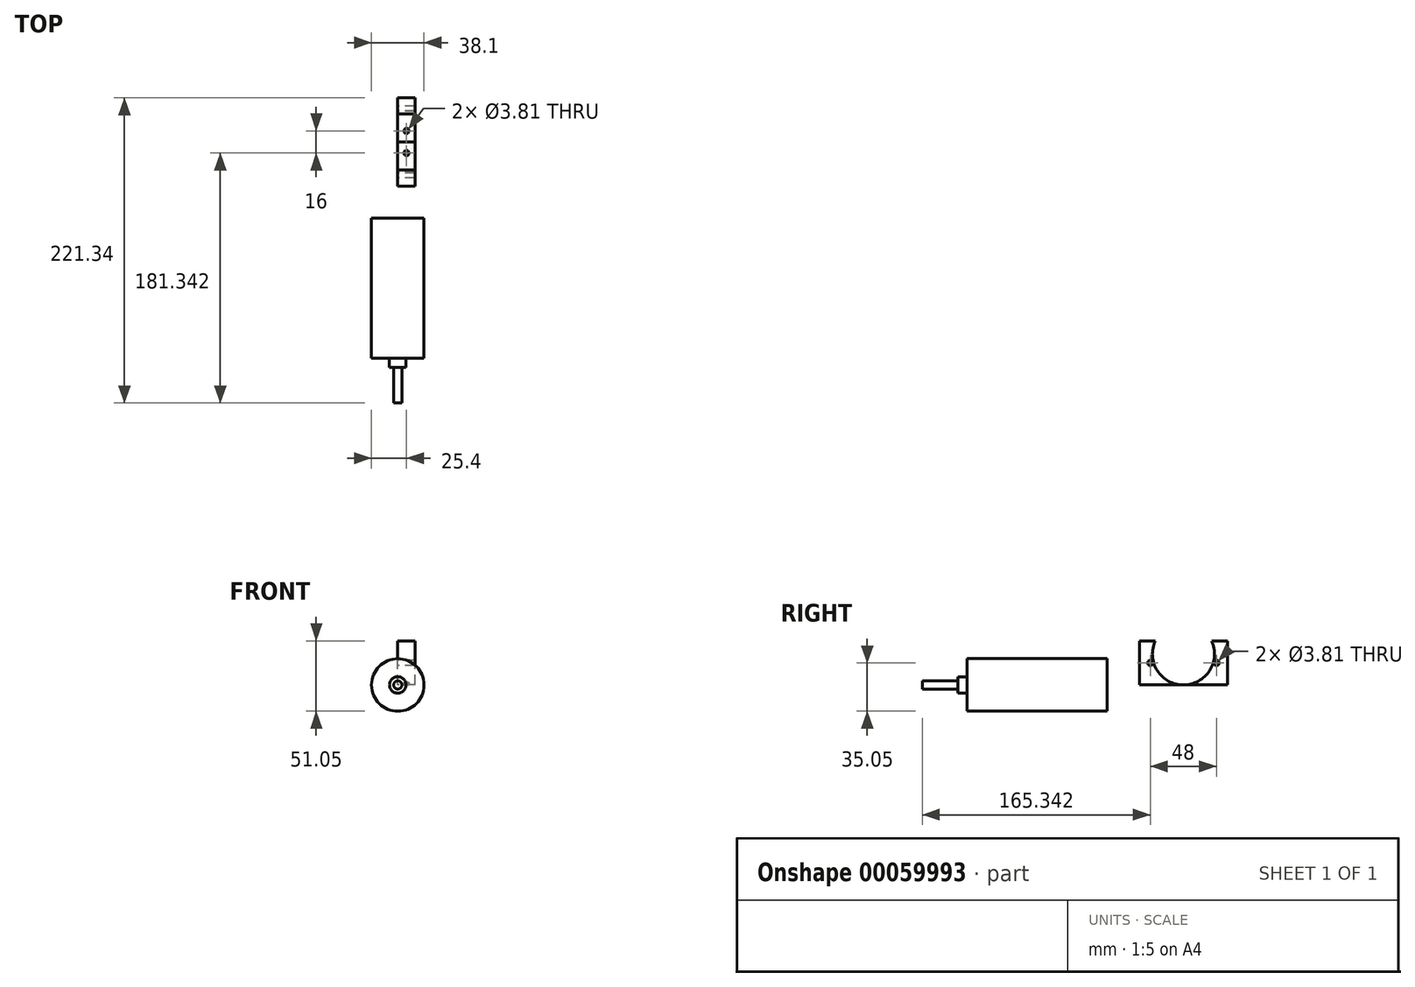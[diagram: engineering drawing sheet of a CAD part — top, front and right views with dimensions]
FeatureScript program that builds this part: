
annotation { "Feature Type Name" : "Feature", "Feature Type Description" : "" }
export const myFeature = defineFeature(function(context is Context, id is Id, definition is map)
    precondition{}
    {
        {
            var Q0;
            Q0=qCreatedBy(makeId("Front.planeOp"),FACE);
            var sketch = newSketch(context, id + "F0", { "sketchPlane" : qUnion([Q0])});
            skCircle(sketch, "E0", {"center": v(0, 0) * mm, "radius": 19.05 * mm});
            skSolve(sketch);
        }
        {
            var Q0;
            Q0=makeQuery(id+"F0.imprint","IMPRINT",FACE,{"disambiguationData":[TD([[makeQuery(id+"F0.imprint","IMPRINT",EDGE,{"derivedFrom":sQuery(id+"F0.wireOp",EDGE,"E0")}),1.0]])]});
            extrude(context, id + "F1", {"entities" : qUnion([Q0]), "depth" : 101.6 * mm});
        }
        {
            var Q0;
            Q0=makeQuery(id+"F1.opExtrude","CAP_FACE",FACE,{"disambiguationData":[OSD([sQuery(id+"F0.wireOp",EDGE,"E0")])],"isStart":false});
            var sketch = newSketch(context, id + "F2", { "sketchPlane" : qUnion([Q0])});
            skCircle(sketch, "E1", {"center": v(0, 0) * mm, "radius": 6 * mm});
            skSolve(sketch);
        }
        {
            var Q0;
            Q0=makeQuery(id+"F2.imprint","IMPRINT",FACE,{"disambiguationData":[TD([[makeQuery(id+"F2.imprint","IMPRINT",EDGE,{"derivedFrom":sQuery(id+"F2.wireOp",EDGE,"E1")}),1.0]])]});
            extrude(context, id + "F3", {"entities" : qUnion([Q0]), "operationType" : NewBodyOperationType.ADD, "depth" : 6.7 * mm});
        }
        {
            var Q0;
            Q0=makeQuery(id+"F3.opExtrude","CAP_FACE",FACE,{"disambiguationData":[OSD([sQuery(id+"F2.wireOp",EDGE,"E1")])],"isStart":false});
            var sketch = newSketch(context, id + "F4", { "sketchPlane" : qUnion([Q0])});
            skCircle(sketch, "E2", {"center": v(0, 0) * mm, "radius": 3 * mm});
            skSolve(sketch);
        }
        {
            var Q0;
            Q0=qSketchRegion(id+"F4",true);
            extrude(context, id + "F5", {"entities" : qUnion([Q0]), "operationType" : NewBodyOperationType.ADD, "depth" : 25.8 * mm});
        }
        {
            var Q0;
            Q0=qCreatedBy(makeId("Right.planeOp"),FACE);
            var sketch = newSketch(context, id + "F6", { "sketchPlane" : qUnion([Q0])});
            skLineSegment(sketch, "E3.bottom", {"start": v(23.24, 0) * mm, "end": v(87.24, 0) * mm});
            skLineSegment(sketch, "E3.top", {"start": v(23.24, 32) * mm, "end": v(87.24, 32) * mm});
            skLineSegment(sketch, "E3.left", {"start": v(23.24, 0) * mm, "end": v(23.24, 32) * mm});
            skLineSegment(sketch, "E3.right", {"start": v(87.24, 0) * mm, "end": v(87.24, 32) * mm});
            skCircle(sketch, "E4", {"center": v(55.24, 22.5) * mm, "radius": 18.5 * mm});
            skPoint(sketch, "E4.centerSnap0", {"position": v(55.24, 32) * mm});
            skCircle(sketch, "E5", {"center": v(55.24, 22.5) * mm, "radius": 22.5 * mm});
            skCircle(sketch, "E6", {"center": v(31.24, 16) * mm, "radius": 1.9 * mm});
            skPoint(sketch, "E6.centerSnap0", {"position": v(23.24, 16) * mm});
            skCircle(sketch, "E7", {"center": v(79.24, 16) * mm, "radius": 1.9 * mm});
            skPoint(sketch, "E7.centerSnap0", {"position": v(87.24, 16) * mm});
            skSolve(sketch);
        }
        {
            var Q0;
            {var subQ0=sQuery(id+"F6.wireOp",EDGE,"E5");var subQ1=sQuery(id+"F6.wireOp",EDGE,"E3.top");var subQ2=makeQuery(id+"F6.imprint","INTERSECT",VERTEX,{"disambiguationData":[OD(0.0)],"derivedFrom":[subQ1,subQ0]});Q0=makeQuery(id+"F6.imprint","IMPRINT",FACE,{"disambiguationData":[TD([[makeQuery(id+"F6.imprint","IMPRINT",EDGE,{"disambiguationData":[TD([[subQ2,-1.0]])],"derivedFrom":subQ1}),1.0]])]});}
            var Q1;
            {var subQ0=sQuery(id+"F6.wireOp",EDGE,"E5");var subQ2=sQuery(id+"F6.wireOp",EDGE,"E3.top");var subQ3=makeQuery(id+"F6.imprint","INTERSECT",VERTEX,{"disambiguationData":[OD(0.0)],"derivedFrom":[subQ2,subQ0]});Q1=makeQuery(id+"F6.imprint","IMPRINT",FACE,{"disambiguationData":[TD([[makeQuery(id+"F6.imprint","IMPRINT",EDGE,{"disambiguationData":[TD([[subQ3,-1.0]])],"derivedFrom":subQ2}),-1.0]])]});}
            var Q2;
            {var subQ0=sQuery(id+"F6.wireOp",EDGE,"E3.left");Q2=makeQuery(id+"F6.imprint","IMPRINT",FACE,{"disambiguationData":[TD([[makeQuery(id+"F6.imprint","IMPRINT",EDGE,{"derivedFrom":subQ0}),-1.0]])]});}
            var Q3;
            {var subQ0=sQuery(id+"F6.wireOp",EDGE,"E3.right");Q3=makeQuery(id+"F6.imprint","IMPRINT",FACE,{"disambiguationData":[TD([[makeQuery(id+"F6.imprint","IMPRINT",EDGE,{"derivedFrom":subQ0}),1.0]])]});}
            extrude(context, id + "F7", {"entities" : qUnion([Q0, Q1, Q2, Q3]), "depth" : 12.7 * mm});
        }
        {
            var Q0;
            Q0=makeQuery(id+"F7.opExtrude","SWEPT_FACE",FACE,{"disambiguationData":[OSD([sQuery(id+"F6.wireOp",EDGE,"E3.bottom")])]});
            var sketch = newSketch(context, id + "F8", { "sketchPlane" : qUnion([Q0])});
            skCircle(sketch, "E8", {"center": v(6.35, -47.24) * mm, "radius": 1.9 * mm});
            skPoint(sketch, "E8.centerSnap0", {"position": v(6.35, -23.24) * mm});
            skLineSegment(sketch, "E9", {"start": v(12.7, -55.24) * mm, "end": v(0, -55.24) * mm, "construction": true});
            skCircle(sketch, "E10.MirrorC", {"center": v(6.35, -63.24) * mm, "radius": 1.9 * mm});
            skSolve(sketch);
        }
        {
            var Q0;
            Q0 = qSketchRegion(id + "F8", true);
            extrude(context, id + "F9", {"entities" : qUnion([Q0]), "operationType" : NewBodyOperationType.REMOVE, "endBound" : BoundingType.UP_TO_NEXT, "oppositeDirection" : true, "depth" : 25.4 * mm});
        }
    });
